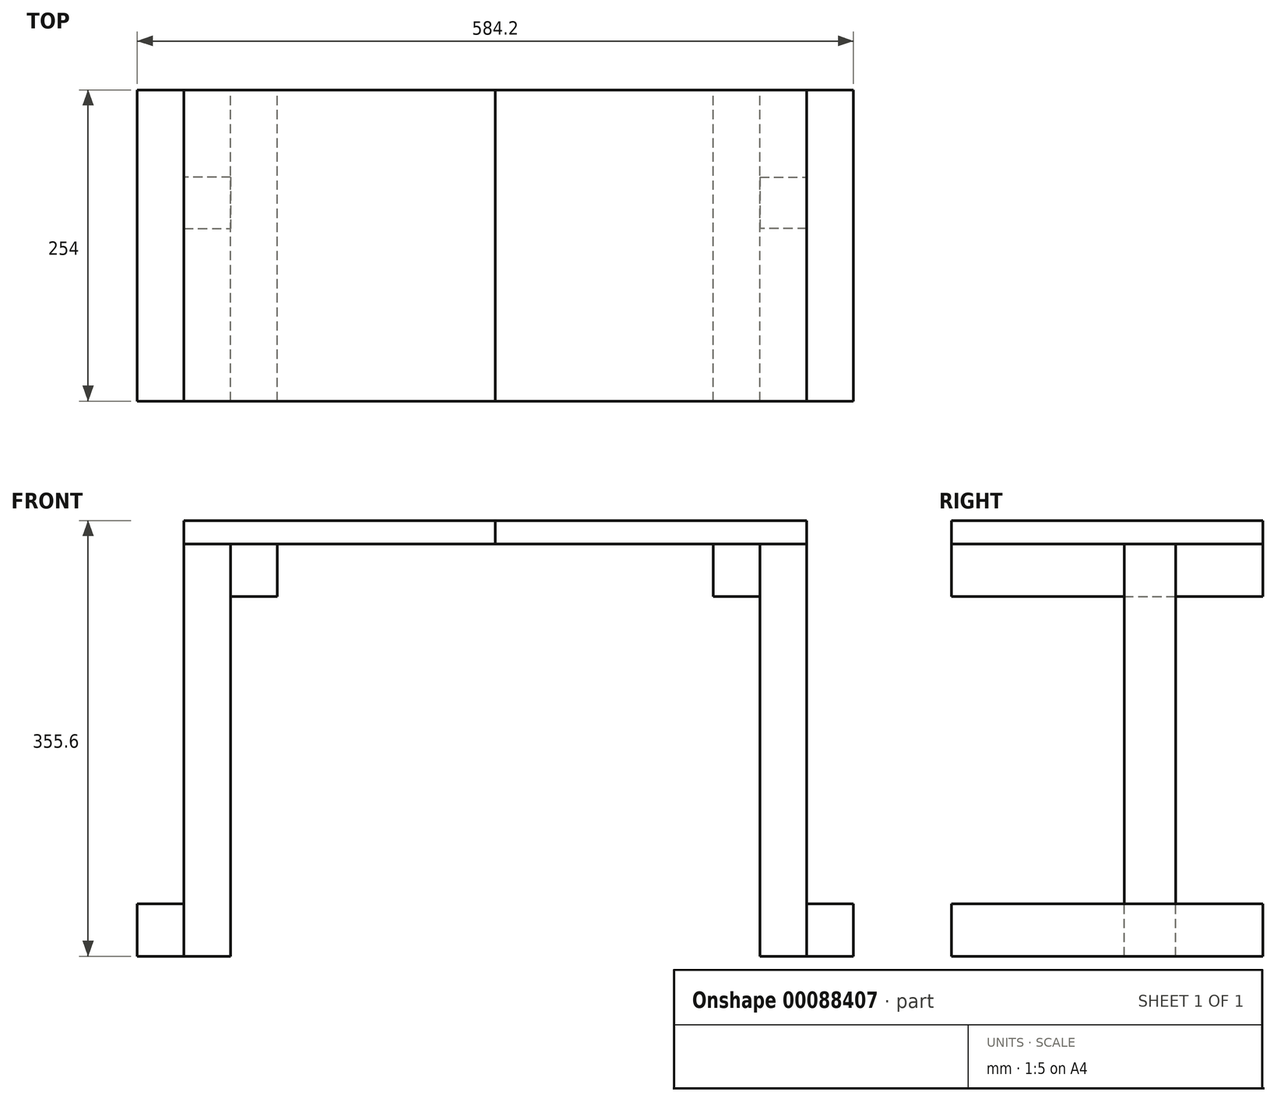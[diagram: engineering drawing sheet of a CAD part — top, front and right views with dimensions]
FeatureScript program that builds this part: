
annotation { "Feature Type Name" : "Feature", "Feature Type Description" : "" }
export const myFeature = defineFeature(function(context is Context, id is Id, definition is map)
    precondition{}
    {
        {
            var Q0;
            Q0=qCreatedBy(makeId("Front.planeOp"),FACE);
            var sketch = newSketch(context, id + "F0", { "sketchPlane" : qUnion([Q0])});
            skLineSegment(sketch, "E0", {"start": v(0, 0) * mm, "end": v(0, 355.6) * mm, "construction": true});
            skSolve(sketch);
        }
        {
            var Q0;
            Q0=qCreatedBy(makeId("Top.planeOp"),FACE);
            var Q1;
            Q1=sQuery(id+"F0.wireOp",VERTEX,"E0.end");
            cPlane(context, id + "F1", {"entities" : qUnion([Q0, Q1]), "cplaneType" : CPlaneType.PLANE_POINT, "offset" : 152.4 * mm, "width" : 152.4 * mm, "height" : 152.4 * mm});
        }
        {
            var Q0;
            Q0=qCreatedBy(id+"F1.planeOp",FACE);
            var sketch = newSketch(context, id + "F2", { "sketchPlane" : qUnion([Q0])});
            skLineSegment(sketch, "E1.bottom", {"start": v(254, 127) * mm, "end": v(0, 127) * mm});
            skLineSegment(sketch, "E1.top", {"start": v(254, -127) * mm, "end": v(0, -127) * mm});
            skLineSegment(sketch, "E1.left", {"start": v(254, 127) * mm, "end": v(254, -127) * mm});
            skLineSegment(sketch, "E1.right", {"start": v(0, 328.9) * mm, "end": v(0, -127) * mm, "construction": true});
            skLineSegment(sketch, "E2", {"start": v(0, -127) * mm, "end": v(0, 127) * mm});
            skSolve(sketch);
        }
        {
            var Q0;
            Q0 = qSketchRegion(id + "F2", true);
            extrude(context, id + "F3", {"entities" : qUnion([Q0]), "oppositeDirection" : true, "depth" : 19.05 * mm});
        }
        {
            var Q0;
            Q0 = qSketchRegion(id + "F2", true);
            extrude(context, id + "F4", {"entities" : qUnion([Q0]), "operationType" : NewBodyOperationType.ADD, "oppositeDirection" : true, "depth" : 19.05 * mm});
        }
        {
            var Q0;
            Q0=makeQuery(id+"F3.opExtrude","CAP_FACE",FACE,{"disambiguationData":[OSD([sQuery(id+"F2.wireOp",EDGE,"E1.bottom"),sQuery(id+"F2.wireOp",EDGE,"E1.top"),sQuery(id+"F2.wireOp",EDGE,"E1.left"),sQuery(id+"F2.wireOp",EDGE,"E2")])],"isStart":false});
            var sketch = newSketch(context, id + "F5", { "sketchPlane" : qUnion([Q0])});
            skLineSegment(sketch, "E3.bottom", {"start": v(254, -127) * mm, "end": v(215.9, -127) * mm, "construction": true});
            skLineSegment(sketch, "E3.top", {"start": v(254, -55.7) * mm, "end": v(215.9, -55.7) * mm});
            skLineSegment(sketch, "E3.left", {"start": v(254, -127) * mm, "end": v(254, -55.7) * mm});
            skLineSegment(sketch, "E3.right", {"start": v(215.9, -127) * mm, "end": v(215.9, 65.64) * mm, "construction": true});
            skLineSegment(sketch, "E4", {"start": v(215.9, -13.86) * mm, "end": v(254, -13.86) * mm});
            skLineSegment(sketch, "E5", {"start": v(254, -13.86) * mm, "end": v(254, -55.7) * mm});
            skLineSegment(sketch, "E6", {"start": v(215.9, -13.86) * mm, "end": v(215.9, -55.7) * mm});
            skSolve(sketch);
        }
        {
            var Q0;
            Q0 = qSketchRegion(id + "F5", true);
            var Q1;
            Q1=qCreatedBy(makeId("Top.planeOp"),FACE);
            extrude(context, id + "F6", {"entities" : qUnion([Q0]), "endBound" : BoundingType.UP_TO_SURFACE, "endBoundEntityFace" : qUnion([Q1]), "depth" : 25.4 * mm});
        }
        {
            var Q0;
            Q0=makeQuery(id+"F6.boolean.opBoolean","MERGE",FACE,{"derivedFrom":[makeQuery(id+"F3.opExtrude","SWEPT_FACE",FACE,{"disambiguationData":[OSD([sQuery(id+"F2.wireOp",EDGE,"E1.bottom")])]}),makeQuery(id+"F6.opExtrude","SWEPT_FACE",FACE,{"disambiguationData":[OSD([sQuery(id+"F5.wireOp",EDGE,"E3.bottom")])]})]});
            var sketch = newSketch(context, id + "F7", { "sketchPlane" : qUnion([Q0])});
            skLineSegment(sketch, "E7.bottom", {"start": v(-215.9, 336.55) * mm, "end": v(-177.8, 336.55) * mm});
            skLineSegment(sketch, "E7.top", {"start": v(-215.9, 293.67) * mm, "end": v(-177.8, 293.67) * mm});
            skLineSegment(sketch, "E7.left", {"start": v(-215.9, 336.55) * mm, "end": v(-215.9, 293.67) * mm});
            skLineSegment(sketch, "E7.right", {"start": v(-177.8, 336.55) * mm, "end": v(-177.8, 293.67) * mm});
            skSolve(sketch);
        }
        {
            var Q0;
            Q0 = qSketchRegion(id + "F7", true);
            var Q1;
            Q1=makeQuery(id+"F3.opExtrude","SWEPT_FACE",FACE,{"disambiguationData":[OSD([sQuery(id+"F2.wireOp",EDGE,"E1.top")])]});
            extrude(context, id + "F8", {"entities" : qUnion([Q0]), "endBound" : BoundingType.UP_TO_SURFACE, "oppositeDirection" : true, "endBoundEntityFace" : qUnion([Q1]), "depth" : 25.4 * mm});
        }
        {
            var Q0;
            Q0=makeQuery(id+"F8.opExtrude","CAP_FACE",FACE,{"disambiguationData":[OSD([sQuery(id+"F7.wireOp",EDGE,"E7.bottom"),sQuery(id+"F7.wireOp",EDGE,"E7.top"),sQuery(id+"F7.wireOp",EDGE,"E7.left"),sQuery(id+"F7.wireOp",EDGE,"E7.right")])],"isStart":true});
            var sketch = newSketch(context, id + "F9", { "sketchPlane" : qUnion([Q0])});
            skPoint(sketch, "E8.0", {"position": v(-254, 0) * mm});
            skLineSegment(sketch, "E9.bottom", {"start": v(-254, 0) * mm, "end": v(-292.1, 0) * mm});
            skLineSegment(sketch, "E9.top", {"start": v(-254, 42.88) * mm, "end": v(-292.1, 42.88) * mm});
            skLineSegment(sketch, "E9.left", {"start": v(-254, 0) * mm, "end": v(-254, 42.88) * mm});
            skLineSegment(sketch, "E9.right", {"start": v(-292.1, 0) * mm, "end": v(-292.1, 42.88) * mm});
            skSolve(sketch);
        }
        {
            var Q0;
            Q0 = qSketchRegion(id + "F9", true);
            var Q1;
            Q1=makeQuery(id+"F8.opExtrude","CAP_FACE",FACE,{"disambiguationData":[OSD([sQuery(id+"F7.wireOp",EDGE,"E7.bottom"),sQuery(id+"F7.wireOp",EDGE,"E7.top"),sQuery(id+"F7.wireOp",EDGE,"E7.left"),sQuery(id+"F7.wireOp",EDGE,"E7.right")])],"isStart":false});
            extrude(context, id + "F10", {"entities" : qUnion([Q0]), "endBound" : BoundingType.UP_TO_SURFACE, "oppositeDirection" : true, "endBoundEntityFace" : qUnion([Q1]), "depth" : 25.4 * mm});
        }
        {
            var Q0;
            Q0=makeQuery(id+"F3.opExtrude","SWEPT_BODY",BODY,{"disambiguationData":[OSD([sQuery(id+"F2.wireOp",EDGE,"E1.bottom"),sQuery(id+"F2.wireOp",EDGE,"E1.top"),sQuery(id+"F2.wireOp",EDGE,"E1.left"),sQuery(id+"F2.wireOp",EDGE,"E2")])]});
            var Q1;
            Q1=makeQuery(id+"F6.opExtrude","SWEPT_BODY",BODY,{"disambiguationData":[OSD([sQuery(id+"F5.wireOp",EDGE,"E3.top"),sQuery(id+"F5.wireOp",EDGE,"E4"),sQuery(id+"F5.wireOp",EDGE,"E5"),sQuery(id+"F5.wireOp",EDGE,"E6")])]});
            var Q2;
            Q2=makeQuery(id+"F8.opExtrude","SWEPT_BODY",BODY,{"disambiguationData":[OSD([sQuery(id+"F7.wireOp",EDGE,"E7.bottom"),sQuery(id+"F7.wireOp",EDGE,"E7.top"),sQuery(id+"F7.wireOp",EDGE,"E7.left"),sQuery(id+"F7.wireOp",EDGE,"E7.right")])]});
            var Q3;
            Q3=makeQuery(id+"F10.opExtrude","SWEPT_BODY",BODY,{"disambiguationData":[OSD([sQuery(id+"F9.wireOp",EDGE,"E9.bottom"),sQuery(id+"F9.wireOp",EDGE,"E9.top"),sQuery(id+"F9.wireOp",EDGE,"E9.left"),sQuery(id+"F9.wireOp",EDGE,"E9.right")])]});
            var Q4;
            Q4=qCreatedBy(makeId("Right.planeOp"),FACE);
            mirror(context, id + "F11", {"entities" : qUnion([Q0, Q1, Q2, Q3]), "mirrorPlane" : qUnion([Q4])});
        }
    });
